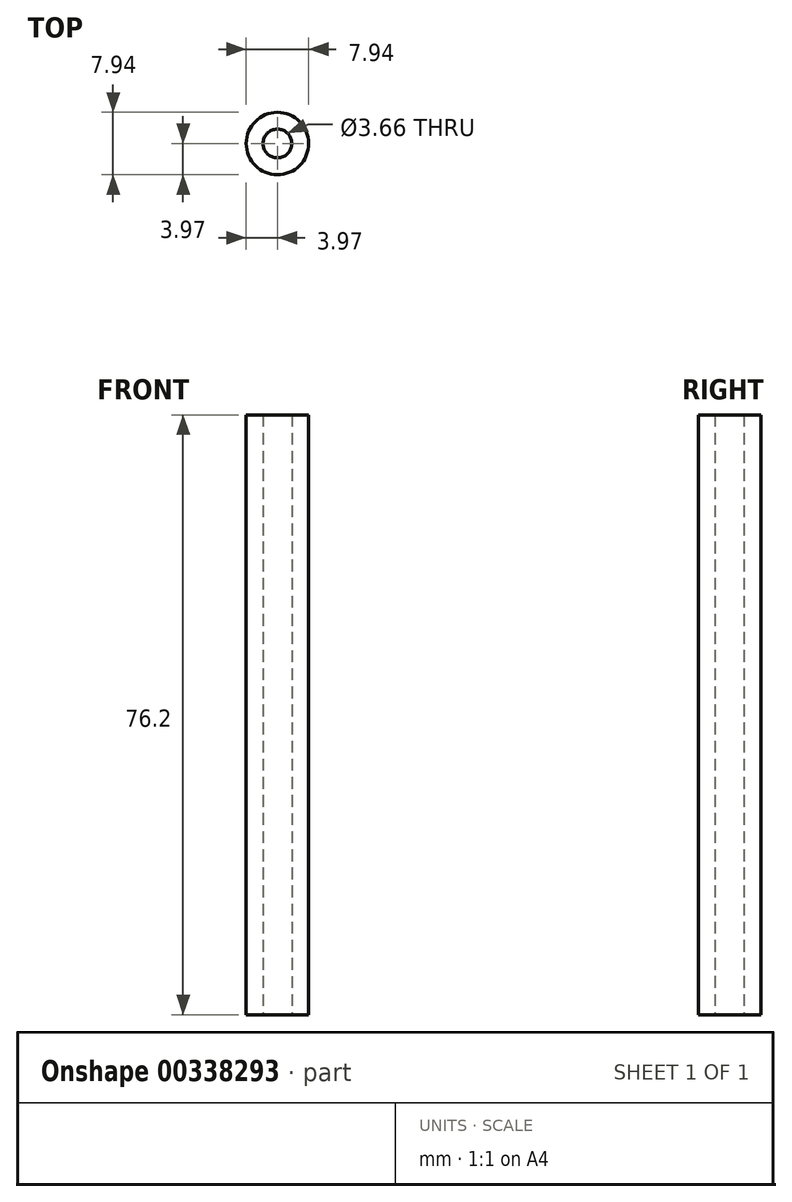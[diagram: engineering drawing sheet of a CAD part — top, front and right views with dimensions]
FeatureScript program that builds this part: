
annotation { "Feature Type Name" : "Feature", "Feature Type Description" : "" }
export const myFeature = defineFeature(function(context is Context, id is Id, definition is map)
    precondition{}
    {
        {
            var Q0;
            Q0=qCreatedBy(makeId("Top.planeOp"),FACE);
            var sketch = newSketch(context, id + "F0", { "sketchPlane" : qUnion([Q0])});
            skCircle(sketch, "E0", {"center": v(0, 0) * mm, "radius": 1.83 * mm});
            skCircle(sketch, "E1", {"center": v(0, 0) * mm, "radius": 3.97 * mm});
            skSolve(sketch);
        }
        {
            var Q0;
            Q0 = qSketchRegion(id + "F0", true);
            extrude(context, id + "F1", {"entities" : qUnion([Q0]), "depth" : 76.2 * mm});
        }
    });
